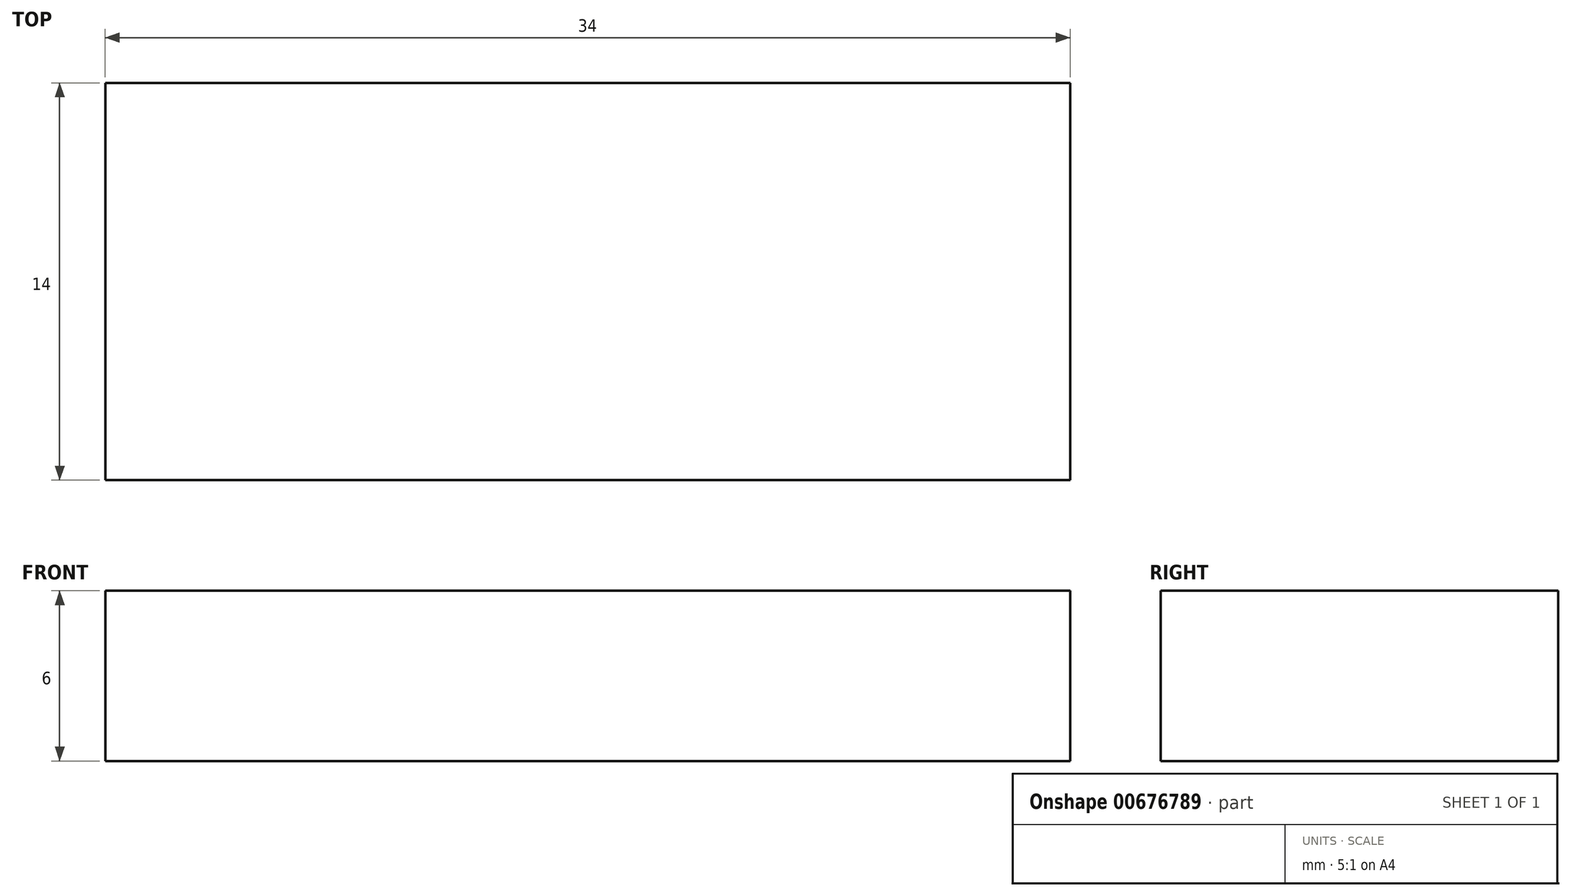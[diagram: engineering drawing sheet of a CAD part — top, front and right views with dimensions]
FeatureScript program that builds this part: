
annotation { "Feature Type Name" : "Feature", "Feature Type Description" : "" }
export const myFeature = defineFeature(function(context is Context, id is Id, definition is map)
    precondition{}
    {
        {
            var Q0;
            Q0=qCreatedBy(makeId("Top.planeOp"),FACE);
            var sketch = newSketch(context, id + "F0", { "sketchPlane" : qUnion([Q0])});
            skLineSegment(sketch, "E0.bottom", {"start": v(-4.62, 5.8) * mm, "end": v(29.38, 5.8) * mm});
            skLineSegment(sketch, "E0.top", {"start": v(-4.62, -8.2) * mm, "end": v(29.38, -8.2) * mm});
            skLineSegment(sketch, "E0.left", {"start": v(-4.62, 5.8) * mm, "end": v(-4.62, -8.2) * mm});
            skLineSegment(sketch, "E0.right", {"start": v(29.38, 5.8) * mm, "end": v(29.38, -8.2) * mm});
            skSolve(sketch);
        }
        {
            var Q0;
            Q0=makeQuery(id+"F0.imprint","IMPRINT",FACE,{"disambiguationData":[TD([[makeQuery(id+"F0.imprint","IMPRINT",EDGE,{"derivedFrom":sQuery(id+"F0.wireOp",EDGE,"E0.bottom")}),-1.0]])]});
            extrude(context, id + "F1", {"entities" : qUnion([Q0]), "depth" : 6 * mm, "offsetDistance" : 25 * mm});
        }
    });
